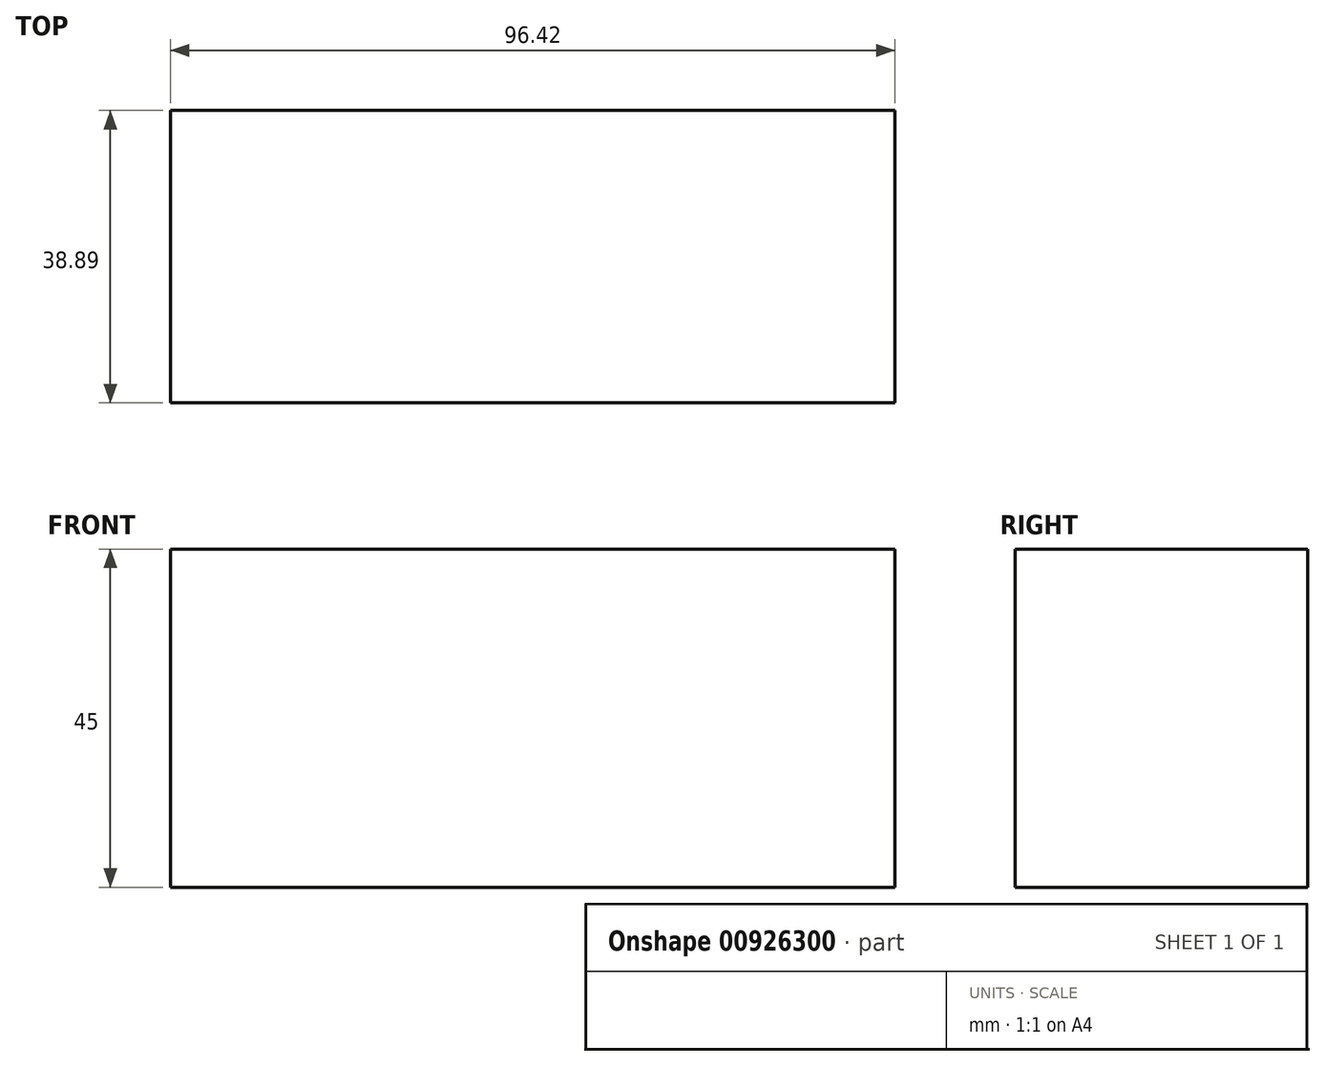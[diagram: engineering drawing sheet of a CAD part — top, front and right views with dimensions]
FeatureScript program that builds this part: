
annotation { "Feature Type Name" : "Feature", "Feature Type Description" : "" }
export const myFeature = defineFeature(function(context is Context, id is Id, definition is map)
    precondition{}
    {
        {
            var Q0;
            Q0=qCreatedBy(makeId("Top.planeOp"),FACE);
            var sketch = newSketch(context, id + "F0", { "sketchPlane" : qUnion([Q0])});
            skLineSegment(sketch, "E0.bottom", {"start": v(-108.32, -17.32) * mm, "end": v(-11.9, -17.32) * mm});
            skLineSegment(sketch, "E0.top", {"start": v(-108.32, 21.57) * mm, "end": v(-11.9, 21.57) * mm});
            skLineSegment(sketch, "E0.left", {"start": v(-108.32, -17.32) * mm, "end": v(-108.32, 21.57) * mm});
            skLineSegment(sketch, "E0.right", {"start": v(-11.9, -17.32) * mm, "end": v(-11.9, 21.57) * mm});
            skSolve(sketch);
        }
        {
            var Q0;
            Q0 = qSketchRegion(id + "F0", true);
            var Q1;
            Q1=makeQuery(id+"F0.imprint","IMPRINT",FACE,{"disambiguationData":[TD([[makeQuery(id+"F0.imprint","IMPRINT",EDGE,{"derivedFrom":sQuery(id+"F0.wireOp",EDGE,"E0.bottom")}),1.0]])]});
            extrude(context, id + "F1", {"entities" : qUnion([Q0, Q1]), "depth" : 20 * mm, "offsetDistance" : 25.4 * mm});
        }
        {
            var Q0;
            Q0=makeQuery(id+"F1.opExtrude","CAP_FACE",FACE,{"disambiguationData":[OSD([sQuery(id+"F0.wireOp",EDGE,"E0.bottom"),sQuery(id+"F0.wireOp",EDGE,"E0.top"),sQuery(id+"F0.wireOp",EDGE,"E0.left"),sQuery(id+"F0.wireOp",EDGE,"E0.right")])],"isStart":false});
            var sketch = newSketch(context, id + "F2", { "sketchPlane" : qUnion([Q0])});
            skCircle(sketch, "E1", {"center": v(-92.1, 0) * mm, "radius": 6.9 * mm});
            skSolve(sketch);
        }
        {
            var Q0;
            Q0 = qSketchRegion(id + "F2", true);
            var Q1;
            Q1=makeQuery(id+"F2.imprint","IMPRINT",FACE,{"disambiguationData":[TD([[makeQuery(id+"F2.imprint","IMPRINT",EDGE,{"derivedFrom":sQuery(id+"F2.wireOp",EDGE,"E1")}),1.0]])]});
            var Q2;
            Q2=makeQuery(id+"F1.opExtrude","CAP_FACE",FACE,{"disambiguationData":[OSD([sQuery(id+"F0.wireOp",EDGE,"E0.bottom"),sQuery(id+"F0.wireOp",EDGE,"E0.top"),sQuery(id+"F0.wireOp",EDGE,"E0.left"),sQuery(id+"F0.wireOp",EDGE,"E0.right")])],"isStart":true});
            extrude(context, id + "F3", {"entities" : qUnion([Q0, Q1, Q2]), "operationType" : NewBodyOperationType.ADD, "oppositeDirection" : true, "depth" : 25 * mm, "offsetDistance" : 25 * mm});
        }
    });
